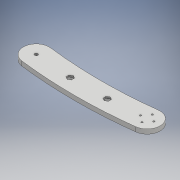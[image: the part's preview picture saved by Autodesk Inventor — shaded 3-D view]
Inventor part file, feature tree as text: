
AUTODESK INVENTOR PART (.ipt)
format: ipt  version: 2017 (Build 210142000, 142)  size: 379,904 bytes
history: native  units: mm
features: sketch x3, extrude x2, chamfer x2, hole x1
ambient origin geometry x8: Origin, YZ Plane, XZ Plane, XY Plane, X Axis, Y Axis, Z Axis, Center Point
bodies: Solid1 (feature_tree)
feature tree (8):
  extrude  "Extrusion1"  Depth=34.6mm
  extrude  "Extrusion2"  Depth=16.0mm
  chamfer  "Chamfer1"  Distance=40.0mm Angle=360.0deg
  hole  "Hole1"  [1 undecoded]
  chamfer  "Chamfer2"  Distance=24.733333mm
  sketch  "Sketch1"  dims[d0=148.4mm d1=34.6mm]
  sketch  "Sketch2"  dims[d2=603.023091mm d3=16.0mm]
  sketch  "Sketch4"  dims[d4=2.3mm d5=40.0mm d7=360.0deg d9=49.466667mm d10=24.733333mm d11=4.3mm d12=4.3mm d13=4.3mm d14=6.0mm d15=0.0mm d16=7.25mm d17=2.0mm d18=0.0mm d19=2.0mm d20=2.0mm d21=45.0deg d22=7.25mm d28=14.48365mm d29=16.0mm d30=2.3mm d31=74.2mm d32=40.0mm d34=360.0deg d36=2.3mm d37=6.0mm d38=4.5mm d39=2.0mm d40=90.0deg d41=8.0mm d42=20.594885mm d43=1.1mm d44=2.0mm d45=45.0deg d46=1.224313mm]
note: 1 required parameter value undecoded (feature->parameter linkage not recoverable at this tier; creation-order binding heuristic only, values carry confidence <= 0.55)
